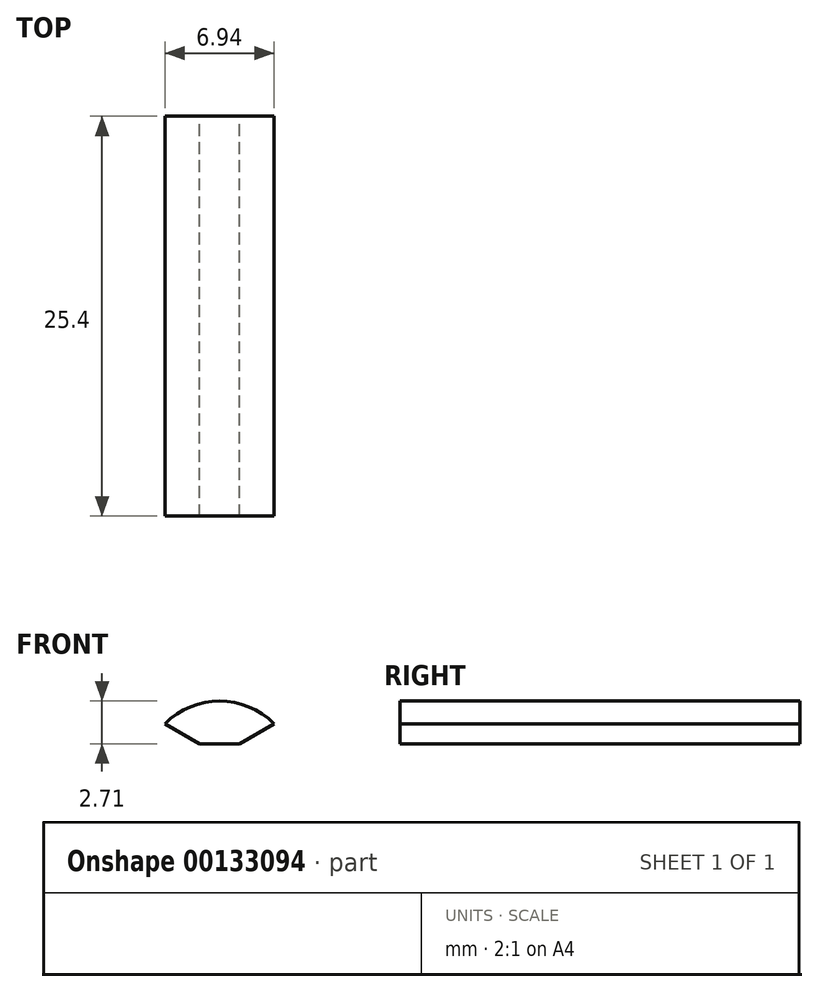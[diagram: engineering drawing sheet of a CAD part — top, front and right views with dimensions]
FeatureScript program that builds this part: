
annotation { "Feature Type Name" : "Feature", "Feature Type Description" : "" }
export const myFeature = defineFeature(function(context is Context, id is Id, definition is map)
    precondition{}
    {
        {
            var Q0;
            Q0=qCreatedBy(makeId("Front.planeOp"),FACE);
            var sketch = newSketch(context, id + "F0", { "sketchPlane" : qUnion([Q0])});
            skLineSegment(sketch, "E0", {"start": v(0, 0) * mm, "end": v(-1.27, 0) * mm});
            skLineSegment(sketch, "E1", {"start": v(-1.27, 0) * mm, "end": v(-3.47, 1.27) * mm});
            skLineSegment(sketch, "E2", {"start": v(0, 0) * mm, "end": v(0, 6.48) * mm, "construction": true});
            skArc(sketch, "E3", {"start": v(0, 2.7) * mm, "mid": v(-1.88, 2.33) * mm, "end": v(-3.47, 1.27) * mm});
            skLineSegment(sketch, "E4", {"start": v(-3.47, 1.27) * mm, "end": v(-2.03, 2.7) * mm, "construction": true});
            skLineSegment(sketch, "E5", {"start": v(-2.03, 2.7) * mm, "end": v(0, 2.7) * mm, "construction": true});
            skArc(sketch, "E6.MirrorCS", {"start": v(0, 2.7) * mm, "mid": v(1.88, 2.33) * mm, "end": v(3.47, 1.27) * mm});
            skLineSegment(sketch, "E7.MirrorCS", {"start": v(1.27, 0) * mm, "end": v(3.47, 1.27) * mm});
            skLineSegment(sketch, "E8.MirrorCS", {"start": v(0, 0) * mm, "end": v(1.27, 0) * mm});
            skSolve(sketch);
        }
        {
            var Q0;
            Q0 = qSketchRegion(id + "F0", true);
            extrude(context, id + "F1", {"entities" : qUnion([Q0]), "depth" : 25.4 * mm});
        }
    });
